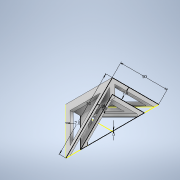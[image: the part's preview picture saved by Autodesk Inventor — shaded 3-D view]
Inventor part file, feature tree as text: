
AUTODESK INVENTOR PART (.ipt)
format: ipt  version: 2020 (Build 240168000, 168)  size: 268,800 bytes
history: native  units: mm
features: sketch x14, extrude x13, plane x5, split x2, shell x2
ambient origin geometry x8: Origin, YZ Plane, XZ Plane, XY Plane, X Axis, Y Axis, Z Axis, Center Point
bodies: Solid1 (feature_tree), Solid4 (feature_tree)
feature tree (36):
  extrude  "Extrusion1"  Depth=2.0mm TaperAngle=0.0deg
  sketch  "Sketch3"  dims[d1=50.0mm d2=2.0mm d3=0.0mm]
  sketch  "Sketch12"  dims[d41=70.71mm d42=50.0mm d43=50.0mm]
  plane  "Work Plane5"
  plane  "Work Plane6"
  extrude  "Extrusion10"  Depth=50.0mm
  split  "Split3"
  shell  "Shell3"  Thickness=50.0mm
  sketch  "Sketch13"  dims[d44=10.0mm d45=0.0mm d46=0.0mm d47=7.8mm]
  plane  "Work Plane9"
  plane  "Work Plane10"
  extrude  "Extrusion18"  TaperAngle=0.0deg  [1 undecoded]
  split  "Split5"
  shell  "Shell5"  Thickness=7.8mm
  extrude  "Extrusion19"  Depth=2.0mm
  extrude  "Extrusion20"  Depth=7.8mm
  extrude  "Extrusion21"  Depth=2.0mm
  extrude  "Extrusion22"  Depth=4.0mm
  extrude  "Extrusion23"  Depth=4.0mm
  extrude  "Extrusion24"  Depth=4.0mm
  plane  "Work Plane11"
  extrude  "Extrusion25"  Depth=4.0mm
  extrude  "Extrusion26"  Depth=2.0mm
  extrude  "Extrusion27"  Depth=4.0mm
  extrude  "Extrusion28"  Depth=2.0mm
  sketch  "Sketch31"  dims[d106=4.0mm d107=4.0mm d108=2.0mm d109=0.0mm d110=2.0mm d111=0.0mm d112=4.0mm d113=0.0mm d114=2.25mm d115=0.0mm d116=2.25mm d117=0.0mm d118=2.25mm d119=0.0mm d120=0.5mm d121=0.872665mm d122=0.5mm d123=0.872665mm]
  sketch  "Sketch20"  dims[d48=7.8mm d49=2.0mm]
  sketch  "Sketch21"  dims[d52=7.8mm d53=7.8mm]
  sketch  "Sketch22"  dims[d85=10.0mm d86=0.0mm d87=2.0mm]
  sketch  "Sketch23"  dims[d88=10.0mm d89=0.0mm d90=4.0mm]
  sketch  "Sketch24"  dims[d91=4.0mm d92=4.0mm]
  sketch  "Sketch25"  dims[d93=2.0mm d94=0.0mm d95=4.0mm]
  sketch  "Sketch27"  dims[d96=4.0mm d97=4.0mm]
  sketch  "Sketch28"  dims[d98=2.0mm d99=0.0mm d100=7.0mm]
  sketch  "Sketch29"  dims[d101=4.0mm d102=4.0mm]
  sketch  "Sketch30"  dims[d103=2.0mm d104=0.0mm d105=7.0mm]
note: 1 required parameter value undecoded (feature->parameter linkage not recoverable at this tier; creation-order binding heuristic only, values carry confidence <= 0.55)
